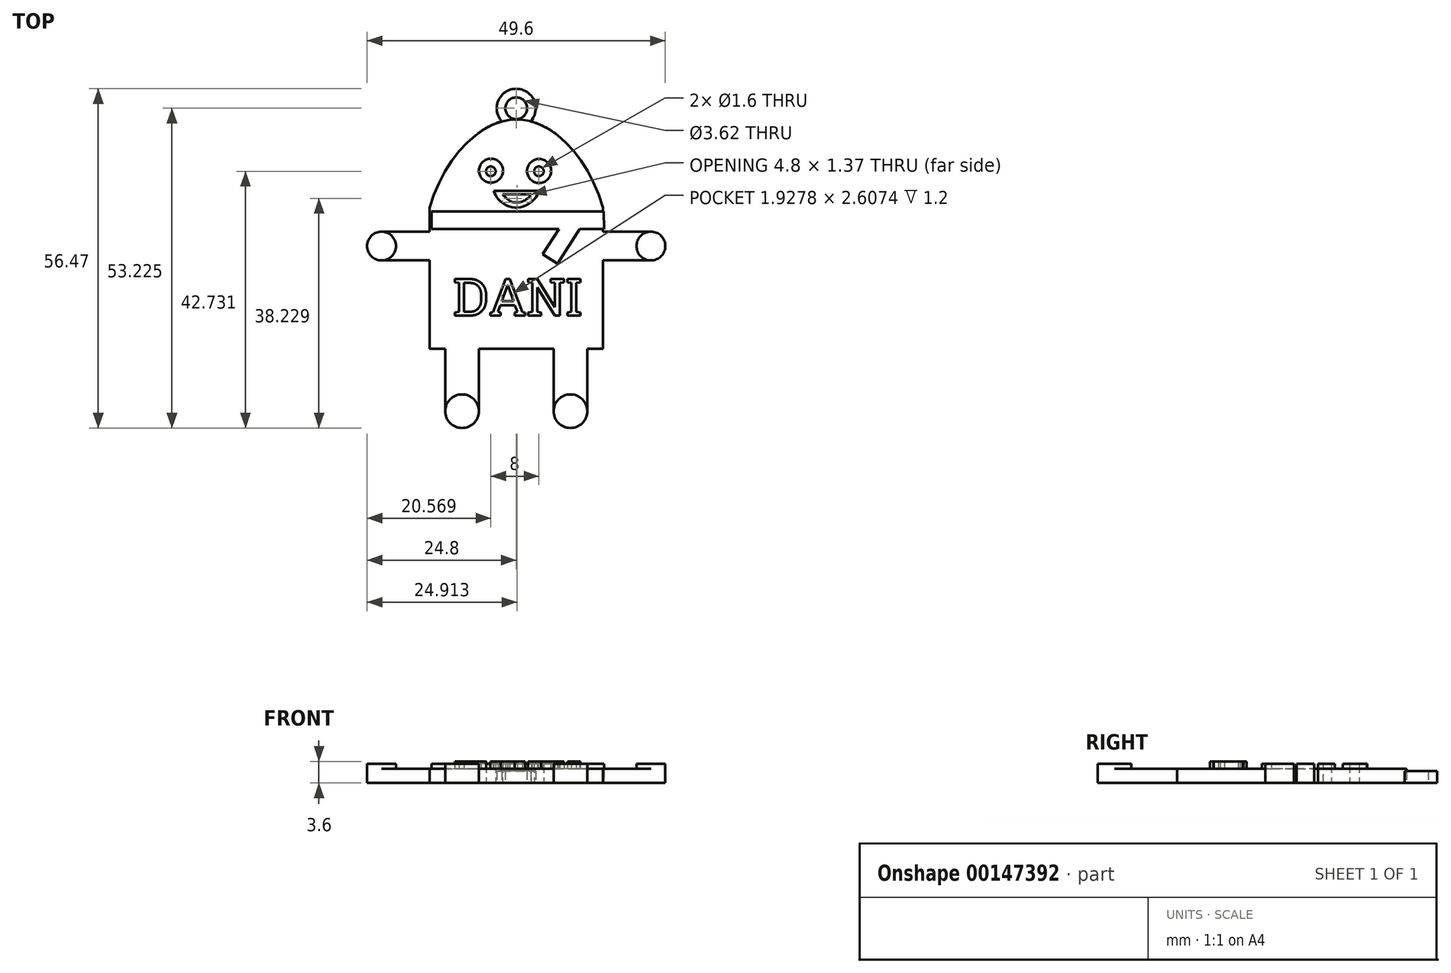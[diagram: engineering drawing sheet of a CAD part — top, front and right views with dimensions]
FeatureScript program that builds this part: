
annotation { "Feature Type Name" : "Feature", "Feature Type Description" : "" }
export const myFeature = defineFeature(function(context is Context, id is Id, definition is map)
    precondition{}
    {
        {
            var Q0;
            Q0=qCreatedBy(makeId("Top.planeOp"),FACE);
            var sketch = newSketch(context, id + "F0", { "sketchPlane" : qUnion([Q0])});
            skLineSegment(sketch, "E0", {"start": v(-18, 0) * mm, "end": v(18, 0) * mm});
            skFitSpline(sketch, "E1", {"points": [v(-18, 0) * mm, v(0, 18.36) * mm, v(18, 0) * mm], "startDerivative": vector(18.37, 62.58) * mm, "endDerivative": vector(17.63, -63.33) * mm});
            skLineSegment(sketch, "E2", {"start": v(-18, 0) * mm, "end": v(-18, -29.37) * mm});
            skLineSegment(sketch, "E3", {"start": v(-18, -29.37) * mm, "end": v(18, -29.37) * mm});
            skLineSegment(sketch, "E4", {"start": v(18, -29.37) * mm, "end": v(18, 0) * mm});
            skLineSegment(sketch, "E5", {"start": v(18, -5) * mm, "end": v(28, -5) * mm});
            skLineSegment(sketch, "E6", {"start": v(28, -5) * mm, "end": v(28, -11) * mm});
            skLineSegment(sketch, "E7", {"start": v(28, -11) * mm, "end": v(18, -11) * mm});
            skLineSegment(sketch, "E8", {"start": v(7.77, -29.37) * mm, "end": v(7.77, -42.37) * mm});
            skLineSegment(sketch, "E9", {"start": v(7.77, -42.37) * mm, "end": v(14.77, -42.37) * mm});
            skLineSegment(sketch, "E10", {"start": v(14.77, -42.37) * mm, "end": v(14.77, -29.37) * mm});
            skLineSegment(sketch, "E11.MirrorCS", {"start": v(-14.77, -42.37) * mm, "end": v(-14.77, -29.37) * mm});
            skLineSegment(sketch, "E12.MirrorCS", {"start": v(-7.77, -42.37) * mm, "end": v(-14.77, -42.37) * mm});
            skLineSegment(sketch, "E13.MirrorCS", {"start": v(-7.77, -29.37) * mm, "end": v(-7.77, -42.37) * mm});
            skCircle(sketch, "E14", {"center": v(28, -8) * mm, "radius": 3 * mm});
            skLineSegment(sketch, "E15.MirrorCS", {"start": v(-28, -11) * mm, "end": v(-18, -11) * mm});
            skLineSegment(sketch, "E16.MirrorCS", {"start": v(-28, -5) * mm, "end": v(-28, -11) * mm});
            skLineSegment(sketch, "E17.MirrorCS", {"start": v(-18, -5) * mm, "end": v(-28, -5) * mm});
            skCircle(sketch, "E18.MirrorC", {"center": v(-28, -8) * mm, "radius": 3 * mm});
            skCircle(sketch, "E19", {"center": v(-11.27, -42.37) * mm, "radius": 3.5 * mm});
            skCircle(sketch, "E20", {"center": v(11.27, -42.37) * mm, "radius": 3.5 * mm});
            skSolve(sketch);
        }
        {
            var Q0;
            Q0 = qSketchRegion(id + "F0", true);
            extrude(context, id + "F1", {"entities" : qUnion([Q0]), "depth" : 3 * mm});
        }
        {
            var Q0;
            Q0=qCreatedBy(makeId("Top.planeOp"),FACE);
            var sketch = newSketch(context, id + "F2", { "sketchPlane" : qUnion([Q0])});
            skCircle(sketch, "E21", {"center": v(-5.25, 7.68) * mm, "radius": 2.5 * mm});
            skCircle(sketch, "E22", {"center": v(4.75, 7.62) * mm, "radius": 2.5 * mm});
            skSolve(sketch);
        }
        {
            var Q0;
            Q0 = qSketchRegion(id + "F2", true);
            extrude(context, id + "F3", {"entities" : qUnion([Q0]), "operationType" : NewBodyOperationType.ADD, "depth" : 4 * mm});
        }
        {
            var Q0;
            Q0=qCreatedBy(makeId("Top.planeOp"),FACE);
            var sketch = newSketch(context, id + "F4", { "sketchPlane" : qUnion([Q0])});
            skLineSegment(sketch, "E23", {"start": v(-4.65, 3.46) * mm, "end": v(4.62, 3.46) * mm});
            skFitSpline(sketch, "E24", {"points": [v(-4.65, 3.46) * mm, v(0, 0) * mm, v(4.62, 3.46) * mm], "startDerivative": vector(2.48, -10.26) * mm, "endDerivative": vector(0.7, 9.57) * mm});
            skSolve(sketch);
        }
        {
            var Q0;
            Q0 = qSketchRegion(id + "F4", true);
            extrude(context, id + "F5", {"entities" : qUnion([Q0]), "operationType" : NewBodyOperationType.ADD, "depth" : 4 * mm});
        }
        {
            var Q0;
            Q0=qCreatedBy(makeId("Top.planeOp"),FACE);
            var sketch = newSketch(context, id + "F6", { "sketchPlane" : qUnion([Q0])});
            skCircle(sketch, "E25", {"center": v(-5.29, 7.55) * mm, "radius": 1 * mm});
            skCircle(sketch, "E26", {"center": v(4.71, 7.55) * mm, "radius": 1 * mm});
            skSolve(sketch);
        }
        {
            var Q0;
            Q0 = qSketchRegion(id + "F6", true);
            extrude(context, id + "F7", {"entities" : qUnion([Q0]), "operationType" : NewBodyOperationType.REMOVE, "depth" : 5 * mm});
        }
        {
            var Q0;
            Q0=qCreatedBy(makeId("Top.planeOp"),FACE);
            var sketch = newSketch(context, id + "F8", { "sketchPlane" : qUnion([Q0])});
            skLineSegment(sketch, "E27", {"start": v(-2.86, 2.78) * mm, "end": v(3.14, 2.78) * mm});
            skFitSpline(sketch, "E28", {"points": [v(-2.86, 2.78) * mm, v(0, 1.07) * mm, v(3.14, 2.78) * mm], "startDerivative": vector(6.43, -7.77) * mm, "endDerivative": vector(5.58, 7.92) * mm});
            skSolve(sketch);
        }
        {
            var Q0;
            Q0 = qSketchRegion(id + "F8", true);
            extrude(context, id + "F9", {"entities" : qUnion([Q0]), "operationType" : NewBodyOperationType.REMOVE, "depth" : 8.25 * mm});
        }
        {
            var Q0;
            Q0=qCreatedBy(makeId("Top.planeOp"),FACE);
            var sketch = newSketch(context, id + "F10", { "sketchPlane" : qUnion([Q0])});
            skCircle(sketch, "E29", {"center": v(0, 20.67) * mm, "radius": 4.06 * mm});
            skCircle(sketch, "E30", {"center": v(0, 20.67) * mm, "radius": 2.26 * mm});
            skSolve(sketch);
        }
        {
            var Q0;
            Q0 = qSketchRegion(id + "F10", true);
            extrude(context, id + "F11", {"entities" : qUnion([Q0]), "operationType" : NewBodyOperationType.ADD, "depth" : 2 * mm});
        }
        {
            var Q0;
            Q0 = qSketchRegion(id + "F10", true);
            extrude(context, id + "F12", {"entities" : qUnion([Q0]), "operationType" : NewBodyOperationType.ADD, "depth" : 2.5 * mm});
        }
        {
            var Q0;
            Q0=qCreatedBy(makeId("Top.planeOp"),FACE);
            var sketch = newSketch(context, id + "F13", { "sketchPlane" : qUnion([Q0])});
            skText(sketch, "E31", { "text": "DANI", "fontName": "RobotoSlab-Regular.ttf"});
            const initialGuessF13  = {"E31": [-0.01311, -0.02247, 1, 0, 0.00769]};
            skSetInitialGuess(sketch, initialGuessF13);
            skSolve(sketch);
        }
        {
            var Q0;
            Q0 = qSketchRegion(id + "F13", true);
            extrude(context, id + "F14", {"entities" : qUnion([Q0]), "operationType" : NewBodyOperationType.ADD, "depth" : 4.5 * mm});
        }
        {
            var Q0;
            Q0=qCreatedBy(makeId("Top.planeOp"),FACE);
            var sketch = newSketch(context, id + "F15", { "sketchPlane" : qUnion([Q0])});
            skLineSegment(sketch, "E32", {"start": v(-17.64, -0.8) * mm, "end": v(18.23, -0.8) * mm});
            skLineSegment(sketch, "E33", {"start": v(-17.64, -0.8) * mm, "end": v(-17.64, -4.44) * mm});
            skLineSegment(sketch, "E34", {"start": v(-17.64, -4.44) * mm, "end": v(18.27, -4.44) * mm});
            skLineSegment(sketch, "E35", {"start": v(18.27, -4.44) * mm, "end": v(18.23, -0.8) * mm});
            skLineSegment(sketch, "E36", {"start": v(8.89, -4.44) * mm, "end": v(5.49, -9.7) * mm});
            skLineSegment(sketch, "E37", {"start": v(5.49, -9.7) * mm, "end": v(8.55, -11.69) * mm});
            skLineSegment(sketch, "E38", {"start": v(8.55, -11.69) * mm, "end": v(13.23, -4.44) * mm});
            skSolve(sketch);
        }
        {
            var Q0;
            Q0 = qSketchRegion(id + "F15", true);
            extrude(context, id + "F16", {"entities" : qUnion([Q0]), "operationType" : NewBodyOperationType.ADD, "depth" : 4 * mm});
        }
        {
            var Q0;
            {var subQ0=sQuery(id+"F0.wireOp",EDGE,"E6");Q0=makeQuery(id+"F0.imprint","IMPRINT",FACE,{"disambiguationData":[TD([[makeQuery(id+"F0.imprint","IMPRINT",EDGE,{"derivedFrom":subQ0}),1.0]])]});}
            var Q1;
            {var subQ0=sQuery(id+"F0.wireOp",EDGE,"E6");Q1=makeQuery(id+"F0.imprint","IMPRINT",FACE,{"disambiguationData":[TD([[makeQuery(id+"F0.imprint","IMPRINT",EDGE,{"derivedFrom":subQ0}),-1.0]])]});}
            var Q2;
            {var subQ0=sQuery(id+"F0.wireOp",EDGE,"E16.MirrorCS");Q2=makeQuery(id+"F0.imprint","IMPRINT",FACE,{"disambiguationData":[TD([[makeQuery(id+"F0.imprint","IMPRINT",EDGE,{"derivedFrom":subQ0}),1.0]])]});}
            var Q3;
            {var subQ0=sQuery(id+"F0.wireOp",EDGE,"E16.MirrorCS");Q3=makeQuery(id+"F0.imprint","IMPRINT",FACE,{"disambiguationData":[TD([[makeQuery(id+"F0.imprint","IMPRINT",EDGE,{"derivedFrom":subQ0}),-1.0]])]});}
            var Q4;
            {var subQ0=sQuery(id+"F0.wireOp",EDGE,"E9");Q4=makeQuery(id+"F0.imprint","IMPRINT",FACE,{"disambiguationData":[TD([[makeQuery(id+"F0.imprint","IMPRINT",EDGE,{"derivedFrom":subQ0}),1.0]])]});}
            var Q5;
            {var subQ0=sQuery(id+"F0.wireOp",EDGE,"E9");Q5=makeQuery(id+"F0.imprint","IMPRINT",FACE,{"disambiguationData":[TD([[makeQuery(id+"F0.imprint","IMPRINT",EDGE,{"derivedFrom":subQ0}),-1.0]])]});}
            var Q6;
            {var subQ0=sQuery(id+"F0.wireOp",EDGE,"E12.MirrorCS");Q6=makeQuery(id+"F0.imprint","IMPRINT",FACE,{"disambiguationData":[TD([[makeQuery(id+"F0.imprint","IMPRINT",EDGE,{"derivedFrom":subQ0}),-1.0]])]});}
            var Q7;
            {var subQ0=sQuery(id+"F0.wireOp",EDGE,"E12.MirrorCS");Q7=makeQuery(id+"F0.imprint","IMPRINT",FACE,{"disambiguationData":[TD([[makeQuery(id+"F0.imprint","IMPRINT",EDGE,{"derivedFrom":subQ0}),1.0]])]});}
            extrude(context, id + "F17", {"entities" : qUnion([Q0, Q1, Q2, Q3, Q4, Q5, Q6, Q7]), "operationType" : NewBodyOperationType.ADD, "depth" : 4 * mm});
        }
        {
            var Q0;
            Q0=makeQuery(id+"F1.opExtrude","SWEPT_BODY",BODY,{"disambiguationData":[OSD([sQuery(id+"F0.wireOp",EDGE,"E1"),sQuery(id+"F0.wireOp",EDGE,"E2"),sQuery(id+"F0.wireOp",EDGE,"E3"),sQuery(id+"F0.wireOp",EDGE,"E4"),sQuery(id+"F0.wireOp",EDGE,"E5"),sQuery(id+"F0.wireOp",EDGE,"E7"),sQuery(id+"F0.wireOp",EDGE,"E8"),sQuery(id+"F0.wireOp",EDGE,"E10"),sQuery(id+"F0.wireOp",EDGE,"E11.MirrorCS"),sQuery(id+"F0.wireOp",EDGE,"E13.MirrorCS"),sQuery(id+"F0.wireOp",EDGE,"E14"),sQuery(id+"F0.wireOp",EDGE,"E15.MirrorCS"),sQuery(id+"F0.wireOp",EDGE,"E17.MirrorCS"),sQuery(id+"F0.wireOp",EDGE,"E18.MirrorC"),sQuery(id+"F0.wireOp",EDGE,"E19"),sQuery(id+"F0.wireOp",EDGE,"E20")])]});
            var Q1;
            Q1=qCreatedBy(makeId("Origin.pointOp"),VERTEX);
            transform(context, id + "F18", {"entities" : qUnion([Q0]), "transformType" : TransformType.SCALE_UNIFORMLY, "scale" : 0.8, "scalePoint" : qUnion([Q1]), "makeCopy" : false});
        }
    });
